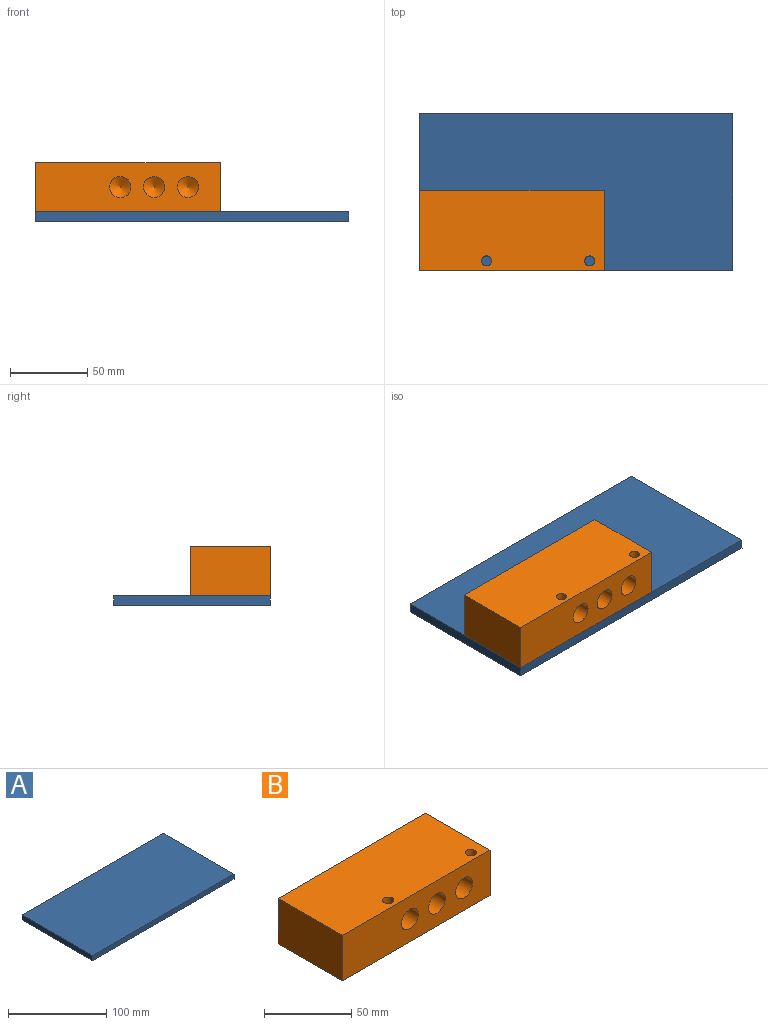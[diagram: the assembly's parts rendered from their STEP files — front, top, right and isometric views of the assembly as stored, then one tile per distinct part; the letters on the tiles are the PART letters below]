
ASSEMBLY  parts=2 mates=1
PART A: 6 faces, bbox 203.2x101.6x6.4 mm
  f0: plane 101.6x6.35mm, normal (1,0,0), area 645.2mm2, adj f1,f3,f4,f5
  f1: plane 203.2x6.35mm, normal (0,1,0), area 1290.3mm2, adj f0,f2,f4,f5
  f2: plane 101.6x6.35mm, normal (-1,0,0), area 645.2mm2, adj f1,f3,f4,f5
  f3: plane 203.2x6.35mm, normal (0,-1,0), area 1290.3mm2, adj f0,f2,f4,f5
  f4: plane 203.2x101.6mm, normal (0,0,1), area 20645.1mm2, adj f0,f1,f2,f3
  f5: plane 203.2x101.6mm, normal (0,0,-1), area 20645.1mm2, adj f0,f1,f2,f3
PART B: 18 faces, bbox 120x52x31.9 mm
  f0: plane 52x31.9mm, normal (-1,0,0), area 1658.9mm2, adj f1,f3,f4,f5
  f1: plane 120x31.9mm, normal (0,-1,0), area 3385mm2, adj f0,f2,f4,f5,f8,f10,f12
  f2: plane 52x31.9mm, normal (1,0,0), area 1658.9mm2, adj f1,f3,f4,f5
  f3: plane 120x31.9mm, normal (0,1,0), area 3532.8mm2, adj f0,f2,f4,f5,f14,f16
  f4: plane 120x52mm, normal (0,0,1), area 6173.6mm2, adj f0,f1,f2,f3,f6,f7
  f5: plane 120x52mm, normal (0,0,-1), area 6173.6mm2, adj f0,f1,f2,f3,f6,f7
  f6: cylinder r=3.25mm len=31.9mm, axis (0,0,-1), area 651.5mm2, adj f4,f5
  f7: cylinder r=3.25mm len=31.9mm, axis (0,0,-1), area 651.5mm2, adj f4,f5
  f8: cylinder r=6.86mm len=16.5mm, axis (0,-1,0), area 711mm2, adj f1,f9
  f9: cone r=0mm half-angle=59deg, axis (0,-1,0), area 172.4mm2, adj f8
  f10: cylinder r=6.86mm len=16.5mm, axis (0,-1,0), area 711mm2, adj f1,f11
  f11: cone r=0mm half-angle=59deg, axis (0,-1,0), area 172.4mm2, adj f10
  f12: cylinder r=6.86mm len=16.5mm, axis (0,-1,0), area 711mm2, adj f1,f13
  f13: cone r=0mm half-angle=59deg, axis (0,-1,0), area 172.4mm2, adj f12
  f14: cylinder r=6.86mm len=16.5mm, axis (0,1,0), area 711mm2, adj f3,f15
  f15: cone r=0mm half-angle=59deg, axis (0,1,0), area 172.4mm2, adj f14
  f16: cylinder r=6.86mm len=16.5mm, axis (0,1,0), area 711mm2, adj f3,f17
  f17: cone r=0mm half-angle=59deg, axis (0,1,0), area 172.4mm2, adj f16
PLACE A rot(axis=(-0.96,-0.21,0.17),0deg) t=(-21.27,7.65,15.5)mm
PLACE B rot(axis=(-0.96,-0.21,0.17),0deg) t=(38.73,33.65,21.85)mm
MATE fastened B.f5 <-> A.f4  axis (0,0,-1) through (-21.27,7.65,21.85)mm
